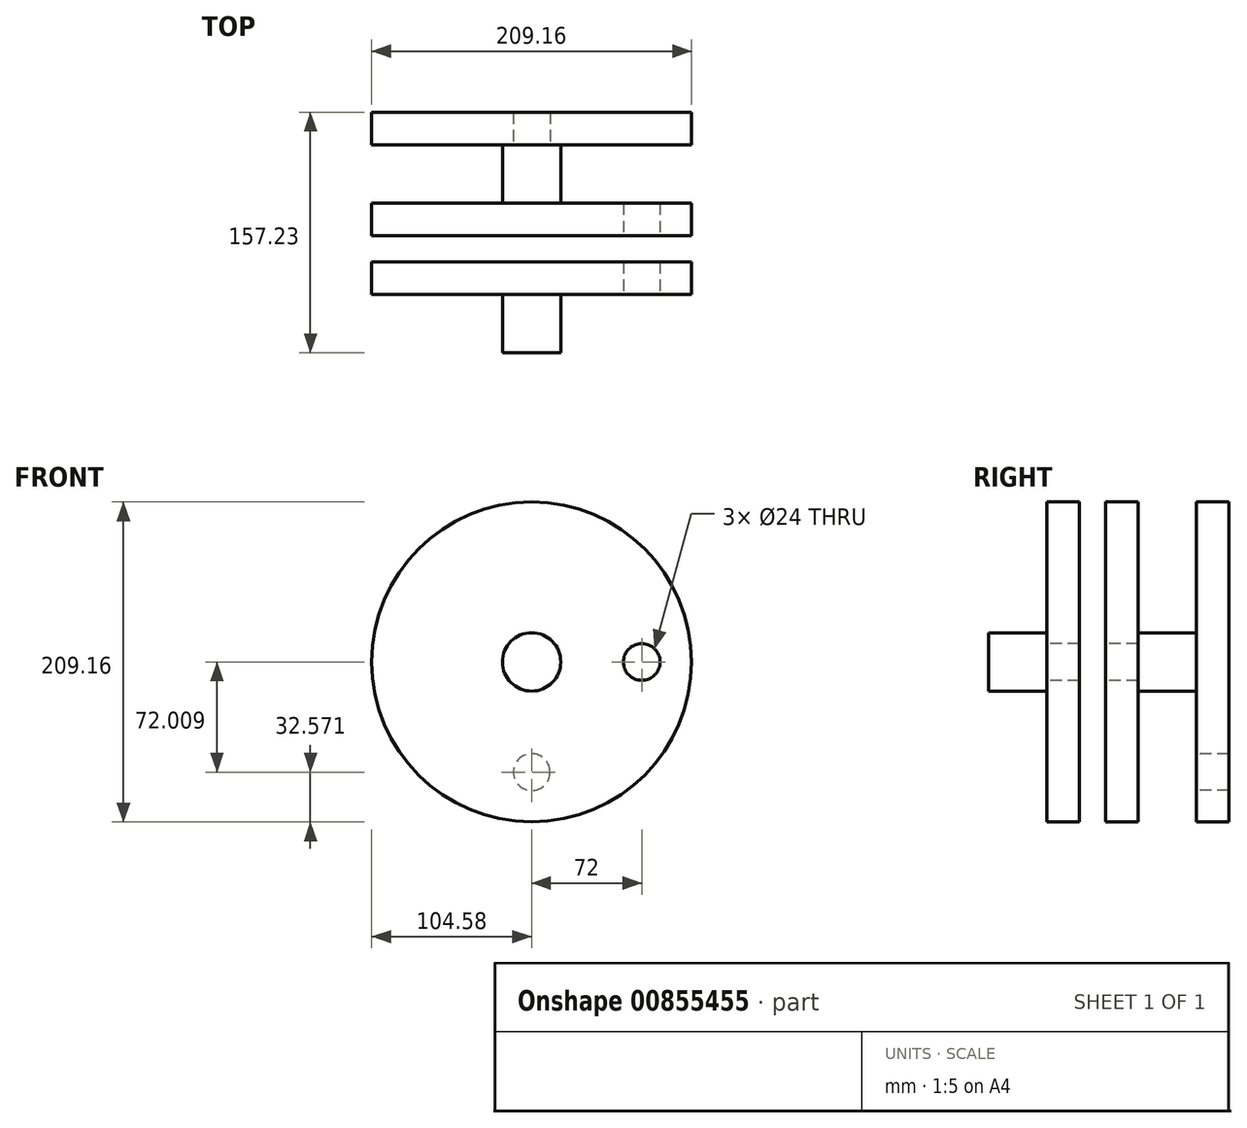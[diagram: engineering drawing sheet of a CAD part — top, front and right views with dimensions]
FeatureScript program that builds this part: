
annotation { "Feature Type Name" : "Feature", "Feature Type Description" : "" }
export const myFeature = defineFeature(function(context is Context, id is Id, definition is map)
    precondition{}
    {
        {
            var Q0;
            Q0=qCreatedBy(makeId("Front.planeOp"),FACE);
            var sketch = newSketch(context, id + "F0", { "sketchPlane" : qUnion([Q0])});
            skCircle(sketch, "E0", {"center": v(0, 0) * mm, "radius": 104.57 * mm});
            skCircle(sketch, "E1", {"center": v(72, 0) * mm, "radius": 12 * mm});
            skPoint(sketch, "E2", {"position": v(84, 0) * mm});
            skPoint(sketch, "E3", {"position": v(104.57, 0) * mm});
            skSolve(sketch);
        }
        {
            var Q0;
            Q0=makeQuery(id+"F0.imprint","IMPRINT",FACE,{"disambiguationData":[TD([[makeQuery(id+"F0.imprint","IMPRINT",EDGE,{"derivedFrom":sQuery(id+"F0.wireOp",EDGE,"E0")}),1.0]])]});
            extrude(context, id + "F1", {"entities" : qUnion([Q0]), "oppositeDirection" : true, "depth" : 21.34 * mm, "offsetDistance" : 25.4 * mm});
        }
        {
            var Q0;
            Q0=makeQuery(id+"F1.opExtrude","CAP_FACE",FACE,{"disambiguationData":[OSD([sQuery(id+"F0.wireOp",EDGE,"E0"),sQuery(id+"F0.wireOp",EDGE,"E1")])],"isStart":true});
            var sketch = newSketch(context, id + "F2", { "sketchPlane" : qUnion([Q0])});
            skCircle(sketch, "E4", {"center": v(0, 0) * mm, "radius": 19.05 * mm});
            skSolve(sketch);
        }
        {
            var Q0;
            Q0=makeQuery(id+"F2.imprint","IMPRINT",FACE,{"disambiguationData":[TD([[makeQuery(id+"F2.imprint","IMPRINT",EDGE,{"derivedFrom":sQuery(id+"F2.wireOp",EDGE,"E4")}),1.0]])]});
            extrude(context, id + "F3", {"entities" : qUnion([Q0]), "operationType" : NewBodyOperationType.ADD, "depth" : 38.1 * mm, "offsetDistance" : 25.4 * mm});
        }
        {
            var Q0;
            Q0=makeQuery(id+"F1.opExtrude","CAP_FACE",FACE,{"disambiguationData":[OSD([sQuery(id+"F0.wireOp",EDGE,"E0"),sQuery(id+"F0.wireOp",EDGE,"E1")])],"isStart":false});
            cPlane(context, id + "F4", {"entities" : qUnion([Q0]), "cplaneType" : CPlaneType.OFFSET, "offset" : 17.02 * mm, "width" : 152.4 * mm, "height" : 152.4 * mm});
        }
        {
            var Q0;
            Q0=qCreatedBy(id+"F4.planeOp",FACE);
            var sketch = newSketch(context, id + "F5", { "sketchPlane" : qUnion([Q0])});
            skCircle(sketch, "E5", {"center": v(0, 0) * mm, "radius": 104.58 * mm});
            skCircle(sketch, "E6", {"center": v(-72, 0) * mm, "radius": 12 * mm});
            skPoint(sketch, "E7", {"position": v(-84, 0) * mm});
            skPoint(sketch, "E8", {"position": v(-104.58, 0) * mm});
            skCircle(sketch, "E9", {"center": v(0, 0) * mm, "radius": 19.05 * mm});
            skSolve(sketch);
        }
        {
            var Q0;
            Q0=makeQuery(id+"F5.imprint","IMPRINT",FACE,{"disambiguationData":[TD([[makeQuery(id+"F5.imprint","IMPRINT",EDGE,{"derivedFrom":sQuery(id+"F5.wireOp",EDGE,"E5")}),1.0]])]});
            extrude(context, id + "F6", {"entities" : qUnion([Q0]), "depth" : 21.34 * mm, "offsetDistance" : 25.4 * mm});
        }
        {
            var Q0;
            Q0=makeQuery(id+"F5.imprint","IMPRINT",FACE,{"disambiguationData":[TD([[makeQuery(id+"F5.imprint","IMPRINT",EDGE,{"derivedFrom":sQuery(id+"F5.wireOp",EDGE,"E9")}),1.0]])]});
            extrude(context, id + "F7", {"entities" : qUnion([Q0]), "operationType" : NewBodyOperationType.ADD, "depth" : 80.77 * mm, "offsetDistance" : 25.4 * mm});
        }
        {
            var Q0;
            Q0=makeQuery(id+"F6.opExtrude","CAP_FACE",FACE,{"disambiguationData":[OSD([sQuery(id+"F5.wireOp",EDGE,"E5"),sQuery(id+"F5.wireOp",EDGE,"E6"),sQuery(id+"F5.wireOp",EDGE,"E9")])],"isStart":false});
            cPlane(context, id + "F8", {"entities" : qUnion([Q0]), "cplaneType" : CPlaneType.OFFSET, "offset" : 38.1 * mm, "width" : 152.4 * mm, "height" : 152.4 * mm});
        }
        {
            var Q0;
            Q0=qCreatedBy(id+"F8.planeOp",FACE);
            var sketch = newSketch(context, id + "F9", { "sketchPlane" : qUnion([Q0])});
            skCircle(sketch, "E10", {"center": v(0, 0) * mm, "radius": 104.58 * mm});
            skCircle(sketch, "E11", {"center": v(0, -72) * mm, "radius": 12 * mm});
            skPoint(sketch, "E12", {"position": v(0, -84.01) * mm});
            skPoint(sketch, "E13", {"position": v(0, -104.58) * mm});
            skSolve(sketch);
        }
        {
            var Q0;
            Q0=makeQuery(id+"F9.imprint","IMPRINT",FACE,{"disambiguationData":[TD([[makeQuery(id+"F9.imprint","IMPRINT",EDGE,{"derivedFrom":sQuery(id+"F9.wireOp",EDGE,"E10")}),1.0]])]});
            extrude(context, id + "F10", {"entities" : qUnion([Q0]), "operationType" : NewBodyOperationType.ADD, "depth" : 21.34 * mm, "offsetDistance" : 25.4 * mm});
        }
    });
